# Revit family: OPTIMA_Compact_Plus_FF_DN50_15_RFA_2018
name_source: partatom
category: Pipe Accessories
revit_build: Autodesk Revit LT 2018 (Build: 20180329_1100(x64)
units: mm (PartAtom-declared; Revit-internal decimal feet)

## family parameters
Always vertical = Yes
Cut with Voids When Loaded = No
Part Type = Valve - Breaks Into
Round Connector Dimension = Use Diameter
Shared = No
Work Plane-Based = No

## types (2) — shared parameters
A = 30.00°
Description = Tlakově nezávislý 2-cestný regulační vyvažovací ventil (PICV)
H1 = 62 mm  [stored 0.203412 ft]
H2 = 15 mm  [stored 0.0492126 ft]
H3 = 35 mm  [stored 0.114829 ft]
H31 = 10 mm  [stored 0.0328084 ft]
H4 = 60 mm  [stored 0.19685 ft]
H5 = 30 mm  [stored 0.0984252 ft]
H51 = 40 mm  [stored 0.131234 ft]
H7 = 86 mm
L1 = 35 mm  [stored 0.114829 ft]
L1__ve = -35 mm  [stored -0.114829 ft]
L2 = 68 mm  [stored 0.223097 ft]
L2D = 138 mm
L2D_Min = 3048 mm  [stored 10 ft]
L3 = 13 mm
L4 = 90 mm  [stored 0.295276 ft]
L5 = 29 mm  [stored 0.0951444 ft]
L6 = 10 mm  [stored 0.0328084 ft]
LL = 69 mm  [stored 0.226378 ft]
Manufacturer = Hydronic Systems Prague s.r.o.
PLG0 = Yes
QmdConnectorList = 301;D;302;D
R3 = 45 mm  [stored 0.147638 ft]
R4 = 34 mm  [stored 0.111549 ft]
R5 = 5 mm  [stored 0.0164042 ft]
R6 = 22 mm  [stored 0.0721785 ft]
R7 = 7 mm  [stored 0.0229659 ft]
R9 = 8 mm  [stored 0.0262467 ft]
S1 = 6 mm  [stored 0.019685 ft]
S2 = 14 mm  [stored 0.0459318 ft]
S3 = 40 mm  [stored 0.131234 ft]
Type Comments = vnitřní závit; PN25; -10~120°C, s měřením
URL = www.hydronic.cz
W2D = 40 mm  [stored 0.131234 ft]
magiPartTypeId = 304
magiProductFamilyId = 6a52986d8e934b98ba96fc38d8cea2

## per-type parameters (varying)
| type | CenSd_R1_6 | D | H6 | H6__ve | MC Product Code | R1 | R2 | X | Z | magiProductId |
| OPTIMA Compact Plus DN40 F-F 15mm | 28 mm | 40 mm | 74 mm  [stored 0.242782 ft] | -74 mm  [stored -0.242782 ft] | 53-1375  (6/4" F-F; 15mm; Qmin-dpmin 1370l/h-10.0kPa; Qmax-dpmin 9500l/h-25.0kPa; dpmax 800kPa) | 32 mm  [stored 0.104987 ft] | 27 mm  [stored 0.0885827 ft] | 15 mm  [stored 0.0492126 ft] | 7 mm  [stored 0.0229659 ft] | 370c574abdd74299b576400338a818 |
| OPTIMA Compact Plus DN50 F-F 15mm | 35 mm  [stored 0.114829 ft] | 50 mm | 82 mm  [stored 0.269029 ft] | -82 mm  [stored -0.269029 ft] | 53-1376  (2" F-F; 15mm; Qmin-dpmin 1400l/h-10.0kPa; Qmax-dpmin 11500l/h-36.0kPa; dpmax 800kPa) | 40 mm  [stored 0.131234 ft] | 34 mm  [stored 0.111549 ft] | 19 mm  [stored 0.062336 ft] | 0 mm  [stored 0 ft] | 624daa8973ca4b919c2525e9502345 |

note: [stored X ft] marks values corroborated as IEEE doubles in the binary element streams (Revit-internal decimal feet)

## geometry (parser evidence)
native form markers: Sweep x1
no freeform markers — native parametric forms only
